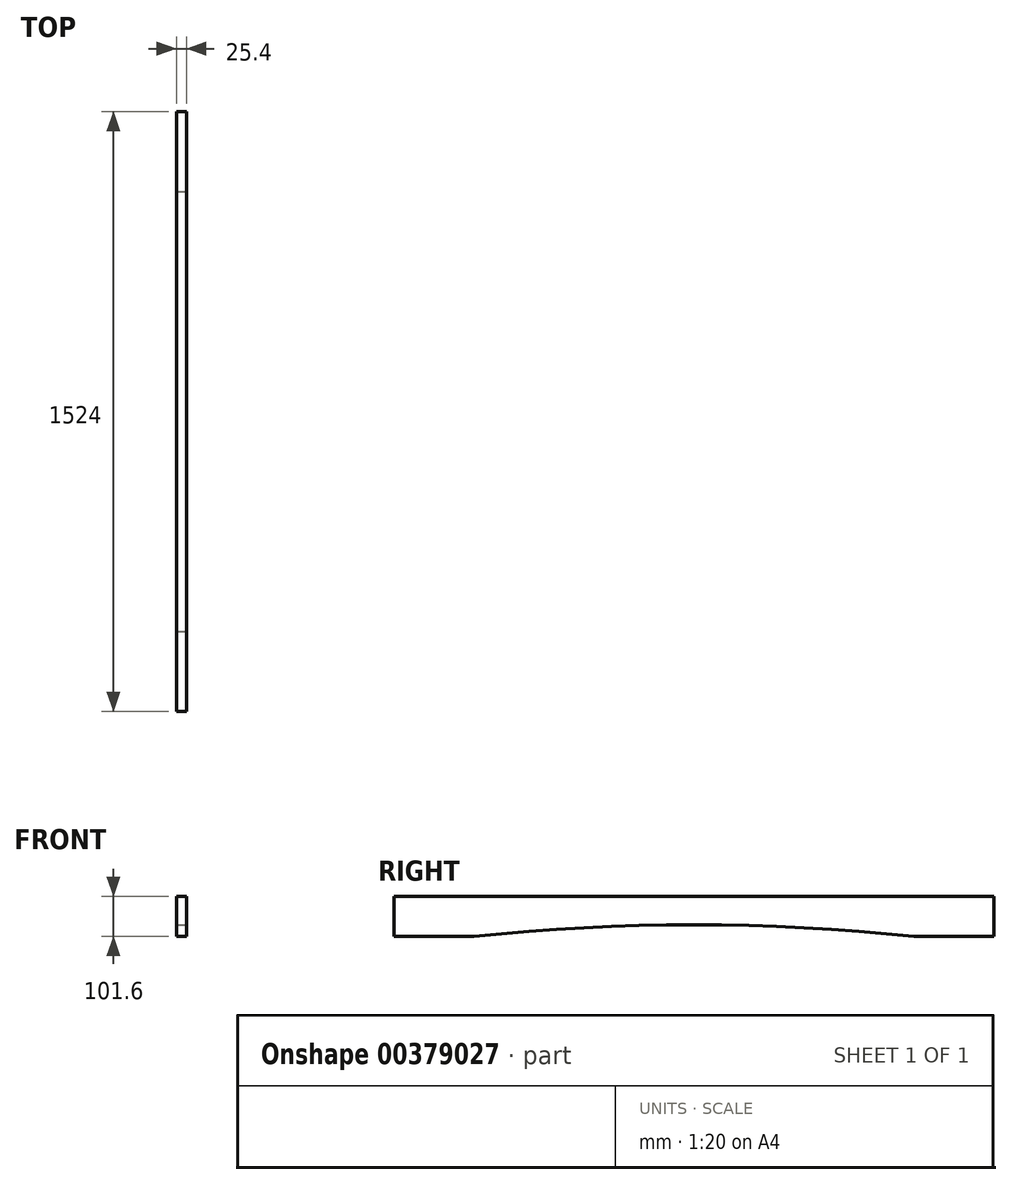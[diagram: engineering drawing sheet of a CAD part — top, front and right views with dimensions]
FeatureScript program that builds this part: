
annotation { "Feature Type Name" : "Feature", "Feature Type Description" : "" }
export const myFeature = defineFeature(function(context is Context, id is Id, definition is map)
    precondition{}
    {
        {
            var Q0;
            Q0=qCreatedBy(makeId("Right.planeOp"),FACE);
            var sketch = newSketch(context, id + "F0", { "sketchPlane" : qUnion([Q0])});
            skLineSegment(sketch, "E0", {"start": v(-721.97, 101.6) * mm, "end": v(802.03, 101.6) * mm});
            skLineSegment(sketch, "E1", {"start": v(-721.97, 101.6) * mm, "end": v(-721.97, 0) * mm});
            skLineSegment(sketch, "E2", {"start": v(802.03, 101.6) * mm, "end": v(802.03, 0) * mm});
            skLineSegment(sketch, "E3", {"start": v(-518.77, 0) * mm, "end": v(-721.97, 0) * mm});
            skLineSegment(sketch, "E4", {"start": v(802.03, 0) * mm, "end": v(598.83, 0) * mm});
            skArc(sketch, "E5", {"start": v(598.83, 0) * mm, "mid": v(40.03, 29.32) * mm, "end": v(-518.77, 0) * mm});
            skSolve(sketch);
        }
        {
            var Q0;
            Q0=makeQuery(id+"F0.imprint","IMPRINT",FACE,{"disambiguationData":[TD([[makeQuery(id+"F0.imprint","IMPRINT",EDGE,{"derivedFrom":sQuery(id+"F0.wireOp",EDGE,"E0")}),-1.0]])]});
            extrude(context, id + "F1", {"entities" : qUnion([Q0]), "oppositeDirection" : true, "depth" : 25.4 * mm});
        }
    });
